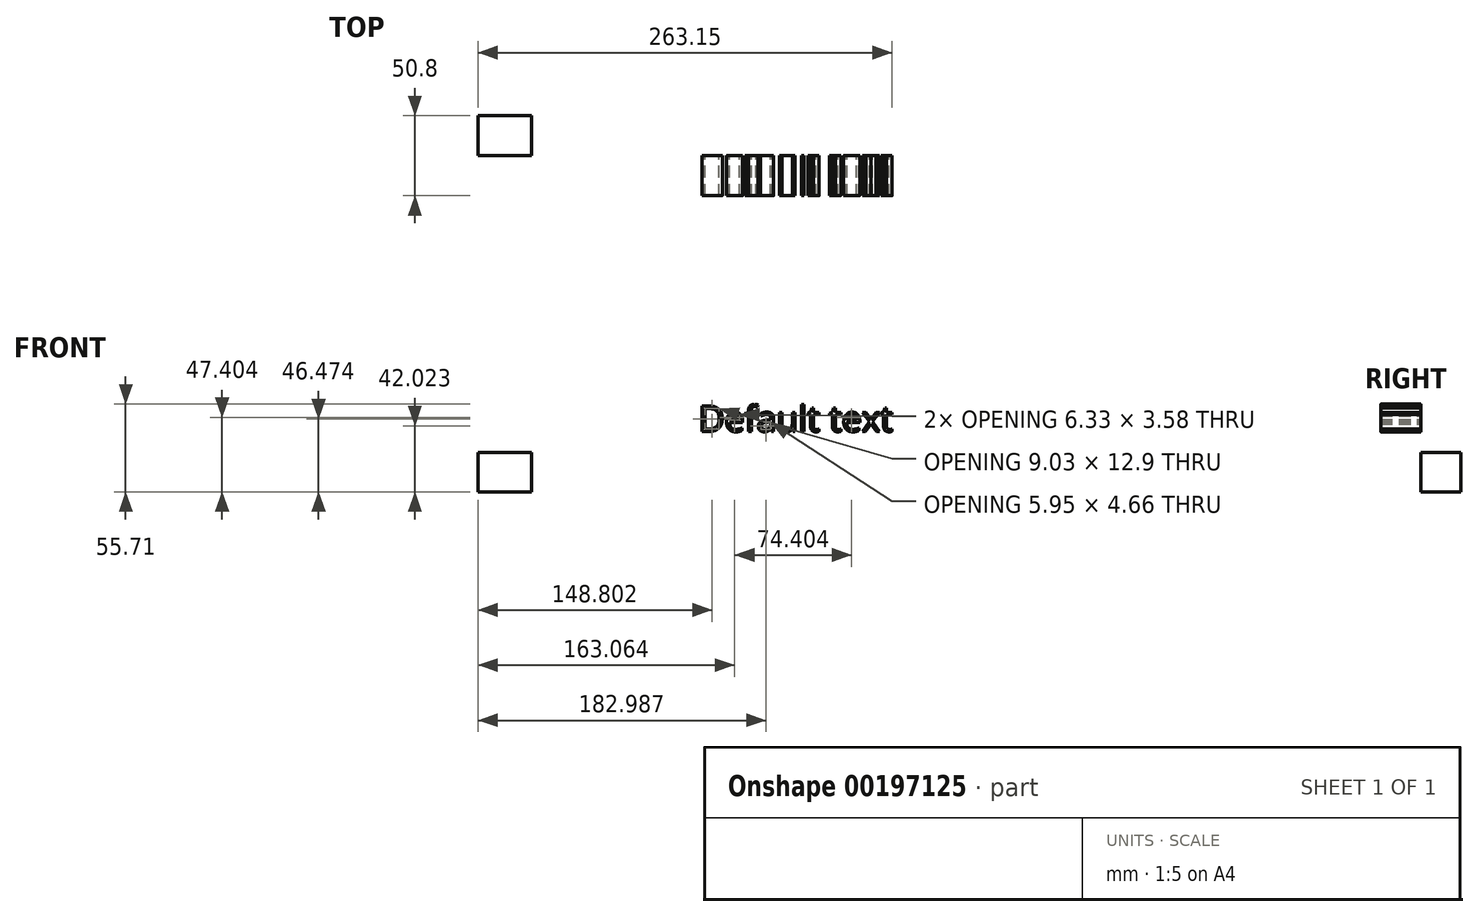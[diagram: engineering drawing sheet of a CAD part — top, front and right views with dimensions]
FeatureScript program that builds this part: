
annotation { "Feature Type Name" : "Feature", "Feature Type Description" : "" }
export const myFeature = defineFeature(function(context is Context, id is Id, definition is map)
    precondition{}
    {
        {
            var Q0;
            Q0=qCreatedBy(makeId("Front.planeOp"),FACE);
            var sketch = newSketch(context, id + "F0", { "sketchPlane" : qUnion([Q0])});
            skLineSegment(sketch, "E0.bottom", {"start": v(-71.12, 41.62) * mm, "end": v(-36.87, 41.62) * mm});
            skLineSegment(sketch, "E0.top", {"start": v(-71.12, 16.54) * mm, "end": v(-36.87, 16.54) * mm});
            skLineSegment(sketch, "E0.left", {"start": v(-71.12, 41.62) * mm, "end": v(-71.12, 16.54) * mm});
            skLineSegment(sketch, "E0.right", {"start": v(-36.87, 41.62) * mm, "end": v(-36.87, 16.54) * mm});
            skSolve(sketch);
        }
        {
            var Q0;
            Q0 = qSketchRegion(id + "F0", true);
            extrude(context, id + "F1", {"entities" : qUnion([Q0]), "depth" : 25.4 * mm});
        }
        {
            var Q0;
            Q0=makeQuery(id+"F1.opExtrude","CAP_FACE",FACE,{"disambiguationData":[OSD([sQuery(id+"F0.wireOp",EDGE,"E0.bottom"),sQuery(id+"F0.wireOp",EDGE,"E0.top"),sQuery(id+"F0.wireOp",EDGE,"E0.left"),sQuery(id+"F0.wireOp",EDGE,"E0.right")])],"isStart":false});
            var sketch = newSketch(context, id + "F2", { "sketchPlane" : qUnion([Q0])});
            skText(sketch, "E1", { "text": "Default text", "fontName": "OpenSans-Regular.ttf"});
            const initialGuessF2  = {"E1": [0.06907, 0.05494, 1, 0, 0.01629]};
            skSetInitialGuess(sketch, initialGuessF2);
            skSolve(sketch);
        }
        {
            var Q0;
            Q0 = qSketchRegion(id + "F2", true);
            extrude(context, id + "F3", {"entities" : qUnion([Q0]), "depth" : 25.4 * mm});
        }
    });
